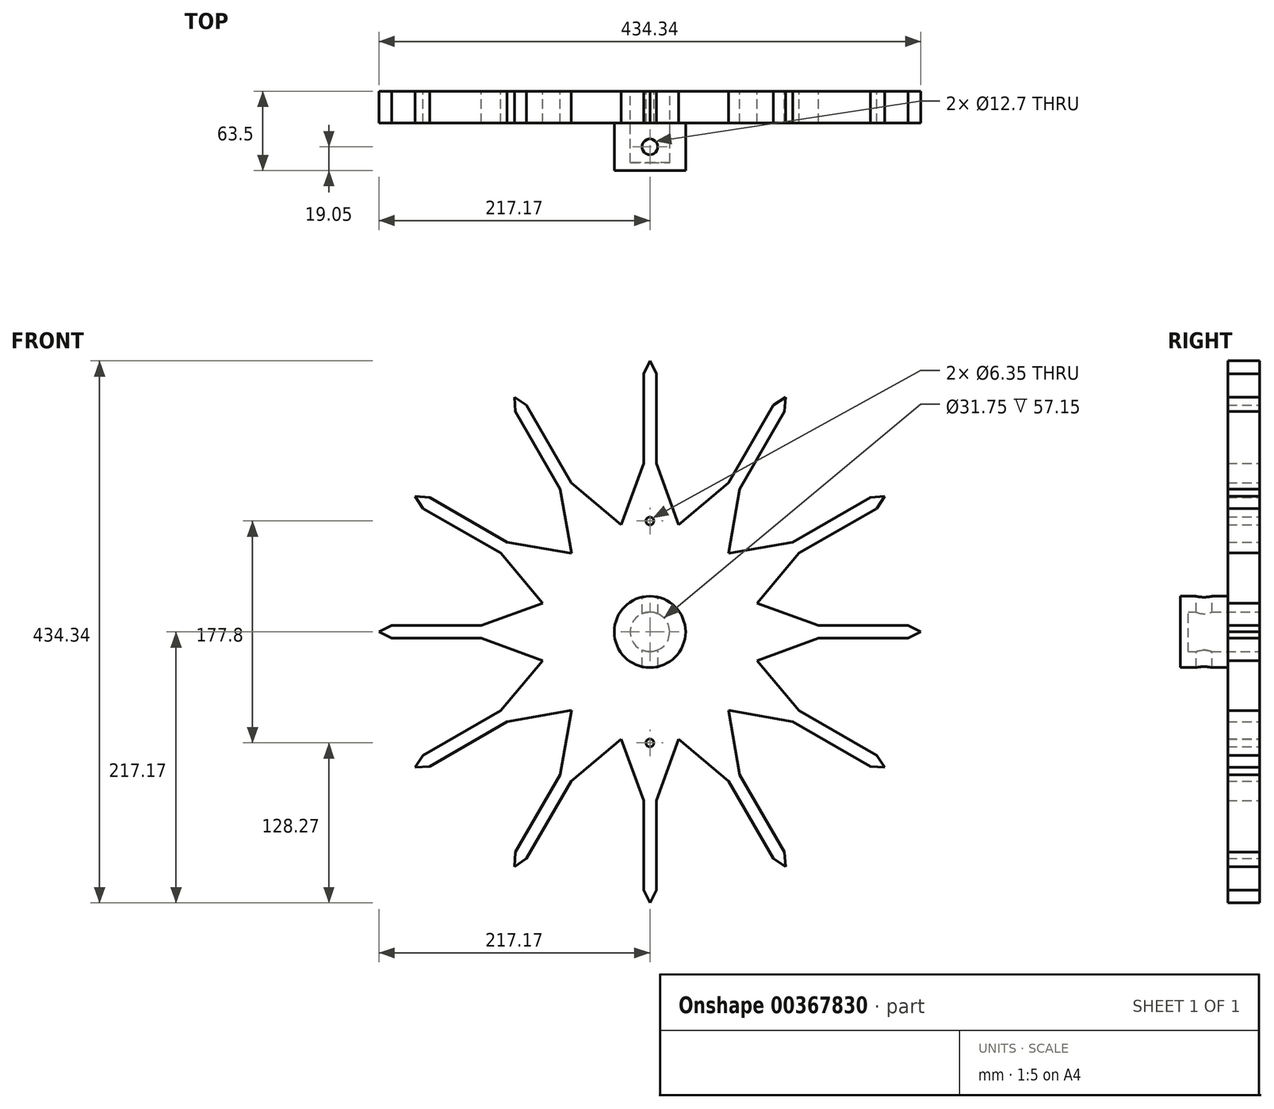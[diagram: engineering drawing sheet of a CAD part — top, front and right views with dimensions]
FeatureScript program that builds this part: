
annotation { "Feature Type Name" : "Feature", "Feature Type Description" : "" }
export const myFeature = defineFeature(function(context is Context, id is Id, definition is map)
    precondition{}
    {
        {
            var Q0;
            Q0=qCreatedBy(makeId("Front.planeOp"),FACE);
            var sketch = newSketch(context, id + "F0", { "sketchPlane" : qUnion([Q0])});
            skCircle(sketch, "E0", {"center": v(0, 0) * mm, "radius": 88.9 * mm});
            skLineSegment(sketch, "E1", {"start": v(0, 88.9) * mm, "end": v(0, 0) * mm, "construction": true});
            skLineSegment(sketch, "E2", {"start": v(44.45, 76.99) * mm, "end": v(0, 0) * mm, "construction": true});
            skLineSegment(sketch, "E3", {"start": v(0, 0) * mm, "end": v(23, 85.87) * mm, "construction": true});
            skCircle(sketch, "E4", {"center": v(0, 0) * mm, "radius": 28.58 * mm});
            skSolve(sketch);
        }
        {
            var Q0;
            Q0=makeQuery(id+"F0.imprint","IMPRINT",FACE,{"disambiguationData":[TD([[makeQuery(id+"F0.imprint","IMPRINT",EDGE,{"derivedFrom":sQuery(id+"F0.wireOp",EDGE,"E0")}),1.0]])]});
            var sketch = newSketch(context, id + "F1", { "sketchPlane" : qUnion([Q0])});
            skLineSegment(sketch, "E5", {"start": v(0, 88.9) * mm, "end": v(0, 217.17) * mm, "construction": true});
            skLineSegment(sketch, "E6.top", {"start": v(5.08, 0) * mm, "end": v(-5.08, 0) * mm});
            skLineSegment(sketch, "E6.left", {"start": v(5.08, 206.78) * mm, "end": v(5.08, 135.13) * mm});
            skLineSegment(sketch, "E6.right", {"start": v(-5.08, 206.78) * mm, "end": v(-5.08, 135.13) * mm});
            skPoint(sketch, "E6.middle", {"position": v(0, 108.59) * mm});
            skLineSegment(sketch, "E7", {"start": v(-5.08, 206.78) * mm, "end": v(0, 217.17) * mm});
            skLineSegment(sketch, "E8", {"start": v(0, 217.17) * mm, "end": v(5.08, 206.78) * mm});
            skPoint(sketch, "E9.orphan", {"position": v(-5.08, 217.17) * mm});
            skPoint(sketch, "E10.orphan", {"position": v(5.08, 217.17) * mm});
            skLineSegment(sketch, "E11", {"start": v(23, 85.87) * mm, "end": v(0, 0) * mm});
            skLineSegment(sketch, "E12", {"start": v(0, 0) * mm, "end": v(0, 108.59) * mm, "construction": true});
            skLineSegment(sketch, "E13", {"start": v(23, 85.87) * mm, "end": v(5.08, 135.13) * mm});
            skLineSegment(sketch, "E14.MirrorCS", {"start": v(-23, 85.87) * mm, "end": v(-5.08, 135.13) * mm});
            skLineSegment(sketch, "E15.MirrorCS", {"start": v(-23, 85.87) * mm, "end": v(0, 0) * mm});
            skLineSegment(sketch, "E16.MirrorCS", {"start": v(-5.08, 0) * mm, "end": v(5.08, 0) * mm});
            skLineSegment(sketch, "E17.MirrorCS", {"start": v(5.08, 206.78) * mm, "end": v(0, 217.17) * mm});
            skLineSegment(sketch, "E18.MirrorCS", {"start": v(0, 217.17) * mm, "end": v(-5.08, 206.78) * mm});
            skPoint(sketch, "E19.orphan", {"position": v(0, 149.09) * mm});
            skLineSegment(sketch, "E20.1.0", {"start": v(-98.99, 181.61) * mm, "end": v(-63.17, 119.57) * mm});
            skLineSegment(sketch, "E20.1.2", {"start": v(-62.86, 62.86) * mm, "end": v(0, 0) * mm});
            skPoint(sketch, "E20.1.3", {"position": v(-112.98, 185.53) * mm});
            skPoint(sketch, "E20.1.4", {"position": v(-104.19, 190.61) * mm});
            skLineSegment(sketch, "E20.1.5", {"start": v(-62.86, 62.86) * mm, "end": v(-71.96, 114.49) * mm});
            skLineSegment(sketch, "E20.1.6", {"start": v(-44.45, 76.99) * mm, "end": v(-108.58, 188.07) * mm, "construction": true});
            skLineSegment(sketch, "E20.1.7", {"start": v(0, 0) * mm, "end": v(-54.3, 94.04) * mm, "construction": true});
            skPoint(sketch, "E20.1.8", {"position": v(-74.54, 129.11) * mm});
            skPoint(sketch, "E20.1.9", {"position": v(-54.3, 94.04) * mm});
            skLineSegment(sketch, "E20.1.10", {"start": v(-107.79, 176.53) * mm, "end": v(-71.96, 114.49) * mm});
            skLineSegment(sketch, "E20.1.11", {"start": v(-98.99, 181.61) * mm, "end": v(-63.17, 119.57) * mm});
            skPoint(sketch, "E20.1.12", {"position": v(-112.98, 185.53) * mm});
            skPoint(sketch, "E20.1.13", {"position": v(-54.3, 94.04) * mm});
            skLineSegment(sketch, "E20.1.15", {"start": v(-62.86, 62.86) * mm, "end": v(0, 0) * mm});
            skLineSegment(sketch, "E20.1.16", {"start": v(-107.79, 176.53) * mm, "end": v(-71.96, 114.49) * mm});
            skPoint(sketch, "E20.1.17", {"position": v(-74.54, 129.11) * mm});
            skLineSegment(sketch, "E20.1.18", {"start": v(0, 0) * mm, "end": v(-54.3, 94.04) * mm, "construction": true});
            skLineSegment(sketch, "E20.1.19", {"start": v(-62.86, 62.86) * mm, "end": v(-71.96, 114.49) * mm});
            skPoint(sketch, "E20.1.20", {"position": v(-104.19, 190.61) * mm});
            skPoint(sketch, "E20.1.21", {"position": v(-74.54, 129.11) * mm});
            skLineSegment(sketch, "E20.1.22", {"start": v(-23, 85.87) * mm, "end": v(-63.17, 119.57) * mm});
            skLineSegment(sketch, "E20.1.23", {"start": v(-23, 85.87) * mm, "end": v(-63.17, 119.57) * mm});
            skPoint(sketch, "E20.1.24", {"position": v(-74.54, 129.11) * mm});
            skLineSegment(sketch, "E20.1.25", {"start": v(-4.4, -2.54) * mm, "end": v(4.4, 2.54) * mm});
            skLineSegment(sketch, "E20.1.26", {"start": v(-98.99, 181.61) * mm, "end": v(-108.59, 188.07) * mm});
            skLineSegment(sketch, "E20.1.27", {"start": v(-107.79, 176.53) * mm, "end": v(-108.58, 188.07) * mm});
            skLineSegment(sketch, "E20.1.28", {"start": v(4.4, 2.54) * mm, "end": v(-4.4, -2.54) * mm});
            skLineSegment(sketch, "E20.1.29", {"start": v(-108.59, 188.07) * mm, "end": v(-107.79, 176.53) * mm});
            skLineSegment(sketch, "E20.1.30", {"start": v(-108.59, 188.07) * mm, "end": v(-98.99, 181.61) * mm});
            skLineSegment(sketch, "E20.2.0", {"start": v(-176.53, 107.79) * mm, "end": v(-114.49, 71.96) * mm});
            skLineSegment(sketch, "E20.2.1", {"start": v(-62.86, 62.86) * mm, "end": v(0, 0) * mm});
            skLineSegment(sketch, "E20.2.2", {"start": v(-85.87, 23) * mm, "end": v(0, 0) * mm});
            skPoint(sketch, "E20.2.3", {"position": v(-190.61, 104.19) * mm});
            skPoint(sketch, "E20.2.4", {"position": v(-185.53, 112.98) * mm});
            skLineSegment(sketch, "E20.2.5", {"start": v(-85.87, 23) * mm, "end": v(-119.57, 63.17) * mm});
            skLineSegment(sketch, "E20.2.6", {"start": v(-76.99, 44.45) * mm, "end": v(-188.07, 108.59) * mm, "construction": true});
            skLineSegment(sketch, "E20.2.7", {"start": v(0, 0) * mm, "end": v(-94.04, 54.3) * mm, "construction": true});
            skPoint(sketch, "E20.2.8", {"position": v(-129.11, 74.54) * mm});
            skPoint(sketch, "E20.2.9", {"position": v(-94.04, 54.3) * mm});
            skLineSegment(sketch, "E20.2.10", {"start": v(-181.61, 98.99) * mm, "end": v(-119.57, 63.17) * mm});
            skLineSegment(sketch, "E20.2.11", {"start": v(-176.53, 107.79) * mm, "end": v(-114.49, 71.96) * mm});
            skPoint(sketch, "E20.2.12", {"position": v(-190.61, 104.19) * mm});
            skPoint(sketch, "E20.2.13", {"position": v(-94.04, 54.3) * mm});
            skLineSegment(sketch, "E20.2.14", {"start": v(-62.86, 62.86) * mm, "end": v(0, 0) * mm});
            skLineSegment(sketch, "E20.2.15", {"start": v(-85.87, 23) * mm, "end": v(0, 0) * mm});
            skLineSegment(sketch, "E20.2.16", {"start": v(-181.61, 98.99) * mm, "end": v(-119.57, 63.17) * mm});
            skPoint(sketch, "E20.2.17", {"position": v(-129.11, 74.54) * mm});
            skLineSegment(sketch, "E20.2.18", {"start": v(0, 0) * mm, "end": v(-94.04, 54.3) * mm, "construction": true});
            skLineSegment(sketch, "E20.2.19", {"start": v(-85.87, 23) * mm, "end": v(-119.57, 63.17) * mm});
            skPoint(sketch, "E20.2.20", {"position": v(-185.53, 112.98) * mm});
            skPoint(sketch, "E20.2.21", {"position": v(-129.11, 74.54) * mm});
            skLineSegment(sketch, "E20.2.22", {"start": v(-62.86, 62.86) * mm, "end": v(-114.49, 71.96) * mm});
            skLineSegment(sketch, "E20.2.23", {"start": v(-62.86, 62.86) * mm, "end": v(-114.49, 71.96) * mm});
            skPoint(sketch, "E20.2.24", {"position": v(-129.11, 74.54) * mm});
            skLineSegment(sketch, "E20.2.25", {"start": v(-2.54, -4.4) * mm, "end": v(2.54, 4.4) * mm});
            skLineSegment(sketch, "E20.2.26", {"start": v(-176.53, 107.79) * mm, "end": v(-188.07, 108.59) * mm});
            skLineSegment(sketch, "E20.2.27", {"start": v(-181.61, 98.99) * mm, "end": v(-188.07, 108.59) * mm});
            skLineSegment(sketch, "E20.2.28", {"start": v(2.54, 4.4) * mm, "end": v(-2.54, -4.4) * mm});
            skLineSegment(sketch, "E20.2.29", {"start": v(-188.07, 108.59) * mm, "end": v(-181.61, 98.99) * mm});
            skLineSegment(sketch, "E20.2.30", {"start": v(-188.07, 108.59) * mm, "end": v(-176.53, 107.79) * mm});
            skLineSegment(sketch, "E20.3.0", {"start": v(-206.78, 5.08) * mm, "end": v(-135.13, 5.08) * mm});
            skLineSegment(sketch, "E20.3.1", {"start": v(-85.87, 23) * mm, "end": v(0, 0) * mm});
            skLineSegment(sketch, "E20.3.2", {"start": v(-85.87, -23) * mm, "end": v(0, 0) * mm});
            skPoint(sketch, "E20.3.3", {"position": v(-217.17, -5.08) * mm});
            skPoint(sketch, "E20.3.4", {"position": v(-217.17, 5.08) * mm});
            skLineSegment(sketch, "E20.3.5", {"start": v(-85.87, -23) * mm, "end": v(-135.13, -5.08) * mm});
            skLineSegment(sketch, "E20.3.6", {"start": v(-88.9, 0) * mm, "end": v(-217.17, 0) * mm, "construction": true});
            skLineSegment(sketch, "E20.3.7", {"start": v(0, 0) * mm, "end": v(-108.59, 0) * mm, "construction": true});
            skPoint(sketch, "E20.3.8", {"position": v(-149.09, 0) * mm});
            skPoint(sketch, "E20.3.9", {"position": v(-108.59, 0) * mm});
            skLineSegment(sketch, "E20.3.10", {"start": v(-206.78, -5.08) * mm, "end": v(-135.13, -5.08) * mm});
            skLineSegment(sketch, "E20.3.11", {"start": v(-206.78, 5.08) * mm, "end": v(-135.13, 5.08) * mm});
            skPoint(sketch, "E20.3.12", {"position": v(-217.17, -5.08) * mm});
            skPoint(sketch, "E20.3.13", {"position": v(-108.59, 0) * mm});
            skLineSegment(sketch, "E20.3.14", {"start": v(-85.87, 23) * mm, "end": v(0, 0) * mm});
            skLineSegment(sketch, "E20.3.15", {"start": v(-85.87, -23) * mm, "end": v(0, 0) * mm});
            skLineSegment(sketch, "E20.3.16", {"start": v(-206.78, -5.08) * mm, "end": v(-135.13, -5.08) * mm});
            skPoint(sketch, "E20.3.17", {"position": v(-149.09, 0) * mm});
            skLineSegment(sketch, "E20.3.18", {"start": v(0, 0) * mm, "end": v(-108.59, 0) * mm, "construction": true});
            skLineSegment(sketch, "E20.3.19", {"start": v(-85.87, -23) * mm, "end": v(-135.13, -5.08) * mm});
            skPoint(sketch, "E20.3.20", {"position": v(-217.17, 5.08) * mm});
            skPoint(sketch, "E20.3.21", {"position": v(-149.09, 0) * mm});
            skLineSegment(sketch, "E20.3.22", {"start": v(-85.87, 23) * mm, "end": v(-135.13, 5.08) * mm});
            skLineSegment(sketch, "E20.3.23", {"start": v(-85.87, 23) * mm, "end": v(-135.13, 5.08) * mm});
            skPoint(sketch, "E20.3.24", {"position": v(-149.09, 0) * mm});
            skLineSegment(sketch, "E20.3.25", {"start": v(0, -5.08) * mm, "end": v(0, 5.08) * mm});
            skLineSegment(sketch, "E20.3.26", {"start": v(-206.78, 5.08) * mm, "end": v(-217.17, 0) * mm});
            skLineSegment(sketch, "E20.3.27", {"start": v(-206.78, -5.08) * mm, "end": v(-217.17, 0) * mm});
            skLineSegment(sketch, "E20.3.28", {"start": v(0, 5.08) * mm, "end": v(0, -5.08) * mm});
            skLineSegment(sketch, "E20.3.29", {"start": v(-217.17, 0) * mm, "end": v(-206.78, -5.08) * mm});
            skLineSegment(sketch, "E20.3.30", {"start": v(-217.17, 0) * mm, "end": v(-206.78, 5.08) * mm});
            skLineSegment(sketch, "E20.4.0", {"start": v(-181.61, -98.99) * mm, "end": v(-119.57, -63.17) * mm});
            skLineSegment(sketch, "E20.4.1", {"start": v(-85.87, -23) * mm, "end": v(0, 0) * mm});
            skLineSegment(sketch, "E20.4.2", {"start": v(-62.86, -62.86) * mm, "end": v(0, 0) * mm});
            skPoint(sketch, "E20.4.3", {"position": v(-185.53, -112.98) * mm});
            skPoint(sketch, "E20.4.4", {"position": v(-190.61, -104.19) * mm});
            skLineSegment(sketch, "E20.4.5", {"start": v(-62.86, -62.86) * mm, "end": v(-114.49, -71.96) * mm});
            skLineSegment(sketch, "E20.4.6", {"start": v(-76.99, -44.45) * mm, "end": v(-188.07, -108.59) * mm, "construction": true});
            skLineSegment(sketch, "E20.4.7", {"start": v(0, 0) * mm, "end": v(-94.04, -54.3) * mm, "construction": true});
            skPoint(sketch, "E20.4.8", {"position": v(-129.11, -74.54) * mm});
            skPoint(sketch, "E20.4.9", {"position": v(-94.04, -54.3) * mm});
            skLineSegment(sketch, "E20.4.10", {"start": v(-176.53, -107.79) * mm, "end": v(-114.49, -71.96) * mm});
            skLineSegment(sketch, "E20.4.11", {"start": v(-181.61, -98.99) * mm, "end": v(-119.57, -63.17) * mm});
            skPoint(sketch, "E20.4.12", {"position": v(-185.53, -112.98) * mm});
            skPoint(sketch, "E20.4.13", {"position": v(-94.04, -54.3) * mm});
            skLineSegment(sketch, "E20.4.14", {"start": v(-85.87, -23) * mm, "end": v(0, 0) * mm});
            skLineSegment(sketch, "E20.4.15", {"start": v(-62.86, -62.86) * mm, "end": v(0, 0) * mm});
            skLineSegment(sketch, "E20.4.16", {"start": v(-176.53, -107.79) * mm, "end": v(-114.49, -71.96) * mm});
            skPoint(sketch, "E20.4.17", {"position": v(-129.11, -74.54) * mm});
            skLineSegment(sketch, "E20.4.18", {"start": v(0, 0) * mm, "end": v(-94.04, -54.3) * mm, "construction": true});
            skLineSegment(sketch, "E20.4.19", {"start": v(-62.86, -62.86) * mm, "end": v(-114.49, -71.96) * mm});
            skPoint(sketch, "E20.4.20", {"position": v(-190.61, -104.19) * mm});
            skPoint(sketch, "E20.4.21", {"position": v(-129.11, -74.54) * mm});
            skLineSegment(sketch, "E20.4.22", {"start": v(-85.87, -23) * mm, "end": v(-119.57, -63.17) * mm});
            skLineSegment(sketch, "E20.4.23", {"start": v(-85.87, -23) * mm, "end": v(-119.57, -63.17) * mm});
            skPoint(sketch, "E20.4.24", {"position": v(-129.11, -74.54) * mm});
            skLineSegment(sketch, "E20.4.25", {"start": v(2.54, -4.4) * mm, "end": v(-2.54, 4.4) * mm});
            skLineSegment(sketch, "E20.4.26", {"start": v(-181.61, -98.99) * mm, "end": v(-188.07, -108.58) * mm});
            skLineSegment(sketch, "E20.4.27", {"start": v(-176.53, -107.79) * mm, "end": v(-188.07, -108.58) * mm});
            skLineSegment(sketch, "E20.4.28", {"start": v(-2.54, 4.4) * mm, "end": v(2.54, -4.4) * mm});
            skLineSegment(sketch, "E20.4.29", {"start": v(-188.07, -108.58) * mm, "end": v(-176.53, -107.79) * mm});
            skLineSegment(sketch, "E20.4.30", {"start": v(-188.07, -108.58) * mm, "end": v(-181.61, -98.99) * mm});
            skLineSegment(sketch, "E20.5.0", {"start": v(-107.79, -176.53) * mm, "end": v(-71.96, -114.49) * mm});
            skLineSegment(sketch, "E20.5.1", {"start": v(-62.86, -62.86) * mm, "end": v(0, 0) * mm});
            skLineSegment(sketch, "E20.5.2", {"start": v(-23, -85.87) * mm, "end": v(0, 0) * mm});
            skPoint(sketch, "E20.5.3", {"position": v(-104.19, -190.61) * mm});
            skPoint(sketch, "E20.5.4", {"position": v(-112.98, -185.53) * mm});
            skLineSegment(sketch, "E20.5.5", {"start": v(-23, -85.87) * mm, "end": v(-63.17, -119.57) * mm});
            skLineSegment(sketch, "E20.5.6", {"start": v(-44.45, -76.99) * mm, "end": v(-108.58, -188.07) * mm, "construction": true});
            skLineSegment(sketch, "E20.5.7", {"start": v(0, 0) * mm, "end": v(-54.3, -94.04) * mm, "construction": true});
            skPoint(sketch, "E20.5.8", {"position": v(-74.54, -129.11) * mm});
            skPoint(sketch, "E20.5.9", {"position": v(-54.3, -94.04) * mm});
            skLineSegment(sketch, "E20.5.10", {"start": v(-98.99, -181.61) * mm, "end": v(-63.17, -119.57) * mm});
            skLineSegment(sketch, "E20.5.11", {"start": v(-107.79, -176.53) * mm, "end": v(-71.96, -114.49) * mm});
            skPoint(sketch, "E20.5.12", {"position": v(-104.19, -190.61) * mm});
            skPoint(sketch, "E20.5.13", {"position": v(-54.3, -94.04) * mm});
            skLineSegment(sketch, "E20.5.14", {"start": v(-62.86, -62.86) * mm, "end": v(0, 0) * mm});
            skLineSegment(sketch, "E20.5.15", {"start": v(-23, -85.87) * mm, "end": v(0, 0) * mm});
            skLineSegment(sketch, "E20.5.16", {"start": v(-98.99, -181.61) * mm, "end": v(-63.17, -119.57) * mm});
            skPoint(sketch, "E20.5.17", {"position": v(-74.54, -129.11) * mm});
            skLineSegment(sketch, "E20.5.18", {"start": v(0, 0) * mm, "end": v(-54.3, -94.04) * mm, "construction": true});
            skLineSegment(sketch, "E20.5.19", {"start": v(-23, -85.87) * mm, "end": v(-63.17, -119.57) * mm});
            skPoint(sketch, "E20.5.20", {"position": v(-112.98, -185.53) * mm});
            skPoint(sketch, "E20.5.21", {"position": v(-74.54, -129.11) * mm});
            skLineSegment(sketch, "E20.5.22", {"start": v(-62.86, -62.86) * mm, "end": v(-71.96, -114.49) * mm});
            skLineSegment(sketch, "E20.5.23", {"start": v(-62.86, -62.86) * mm, "end": v(-71.96, -114.49) * mm});
            skPoint(sketch, "E20.5.24", {"position": v(-74.54, -129.11) * mm});
            skLineSegment(sketch, "E20.5.25", {"start": v(4.4, -2.54) * mm, "end": v(-4.4, 2.54) * mm});
            skLineSegment(sketch, "E20.5.26", {"start": v(-107.79, -176.53) * mm, "end": v(-108.58, -188.07) * mm});
            skLineSegment(sketch, "E20.5.27", {"start": v(-98.99, -181.61) * mm, "end": v(-108.59, -188.07) * mm});
            skLineSegment(sketch, "E20.5.28", {"start": v(-4.4, 2.54) * mm, "end": v(4.4, -2.54) * mm});
            skLineSegment(sketch, "E20.5.29", {"start": v(-108.59, -188.07) * mm, "end": v(-98.99, -181.61) * mm});
            skLineSegment(sketch, "E20.5.30", {"start": v(-108.59, -188.07) * mm, "end": v(-107.79, -176.53) * mm});
            skLineSegment(sketch, "E20.6.0", {"start": v(-5.08, -206.78) * mm, "end": v(-5.08, -135.13) * mm});
            skLineSegment(sketch, "E20.6.1", {"start": v(-23, -85.87) * mm, "end": v(0, 0) * mm});
            skLineSegment(sketch, "E20.6.2", {"start": v(23, -85.87) * mm, "end": v(0, 0) * mm});
            skPoint(sketch, "E20.6.3", {"position": v(5.08, -217.17) * mm});
            skPoint(sketch, "E20.6.4", {"position": v(-5.08, -217.17) * mm});
            skLineSegment(sketch, "E20.6.5", {"start": v(23, -85.87) * mm, "end": v(5.08, -135.13) * mm});
            skLineSegment(sketch, "E20.6.6", {"start": v(0, -88.9) * mm, "end": v(0, -217.17) * mm, "construction": true});
            skLineSegment(sketch, "E20.6.7", {"start": v(0, 0) * mm, "end": v(0, -108.59) * mm, "construction": true});
            skPoint(sketch, "E20.6.8", {"position": v(0, -149.09) * mm});
            skPoint(sketch, "E20.6.9", {"position": v(0, -108.59) * mm});
            skLineSegment(sketch, "E20.6.10", {"start": v(5.08, -206.78) * mm, "end": v(5.08, -135.13) * mm});
            skLineSegment(sketch, "E20.6.11", {"start": v(-5.08, -206.78) * mm, "end": v(-5.08, -135.13) * mm});
            skPoint(sketch, "E20.6.12", {"position": v(5.08, -217.17) * mm});
            skPoint(sketch, "E20.6.13", {"position": v(0, -108.59) * mm});
            skLineSegment(sketch, "E20.6.14", {"start": v(-23, -85.87) * mm, "end": v(0, 0) * mm});
            skLineSegment(sketch, "E20.6.15", {"start": v(23, -85.87) * mm, "end": v(0, 0) * mm});
            skLineSegment(sketch, "E20.6.16", {"start": v(5.08, -206.78) * mm, "end": v(5.08, -135.13) * mm});
            skPoint(sketch, "E20.6.17", {"position": v(0, -149.09) * mm});
            skLineSegment(sketch, "E20.6.18", {"start": v(0, 0) * mm, "end": v(0, -108.59) * mm, "construction": true});
            skLineSegment(sketch, "E20.6.19", {"start": v(23, -85.87) * mm, "end": v(5.08, -135.13) * mm});
            skPoint(sketch, "E20.6.20", {"position": v(-5.08, -217.17) * mm});
            skPoint(sketch, "E20.6.21", {"position": v(0, -149.09) * mm});
            skLineSegment(sketch, "E20.6.22", {"start": v(-23, -85.87) * mm, "end": v(-5.08, -135.13) * mm});
            skLineSegment(sketch, "E20.6.23", {"start": v(-23, -85.87) * mm, "end": v(-5.08, -135.13) * mm});
            skPoint(sketch, "E20.6.24", {"position": v(0, -149.09) * mm});
            skLineSegment(sketch, "E20.6.26", {"start": v(-5.08, -206.78) * mm, "end": v(0, -217.17) * mm});
            skLineSegment(sketch, "E20.6.27", {"start": v(5.08, -206.78) * mm, "end": v(0, -217.17) * mm});
            skLineSegment(sketch, "E20.6.29", {"start": v(0, -217.17) * mm, "end": v(5.08, -206.78) * mm});
            skLineSegment(sketch, "E20.6.30", {"start": v(0, -217.17) * mm, "end": v(-5.08, -206.78) * mm});
            skLineSegment(sketch, "E20.7.0", {"start": v(98.99, -181.61) * mm, "end": v(63.17, -119.57) * mm});
            skLineSegment(sketch, "E20.7.1", {"start": v(23, -85.87) * mm, "end": v(0, 0) * mm});
            skLineSegment(sketch, "E20.7.2", {"start": v(62.86, -62.86) * mm, "end": v(0, 0) * mm});
            skPoint(sketch, "E20.7.3", {"position": v(112.98, -185.53) * mm});
            skPoint(sketch, "E20.7.4", {"position": v(104.19, -190.61) * mm});
            skLineSegment(sketch, "E20.7.5", {"start": v(62.86, -62.86) * mm, "end": v(71.96, -114.49) * mm});
            skLineSegment(sketch, "E20.7.6", {"start": v(44.45, -76.99) * mm, "end": v(108.58, -188.07) * mm, "construction": true});
            skLineSegment(sketch, "E20.7.7", {"start": v(0, 0) * mm, "end": v(54.3, -94.04) * mm, "construction": true});
            skPoint(sketch, "E20.7.8", {"position": v(74.54, -129.11) * mm});
            skPoint(sketch, "E20.7.9", {"position": v(54.3, -94.04) * mm});
            skLineSegment(sketch, "E20.7.10", {"start": v(107.79, -176.53) * mm, "end": v(71.96, -114.49) * mm});
            skLineSegment(sketch, "E20.7.11", {"start": v(98.99, -181.61) * mm, "end": v(63.17, -119.57) * mm});
            skPoint(sketch, "E20.7.12", {"position": v(112.98, -185.53) * mm});
            skPoint(sketch, "E20.7.13", {"position": v(54.3, -94.04) * mm});
            skLineSegment(sketch, "E20.7.14", {"start": v(23, -85.87) * mm, "end": v(0, 0) * mm});
            skLineSegment(sketch, "E20.7.15", {"start": v(62.86, -62.86) * mm, "end": v(0, 0) * mm});
            skLineSegment(sketch, "E20.7.16", {"start": v(107.79, -176.53) * mm, "end": v(71.96, -114.49) * mm});
            skPoint(sketch, "E20.7.17", {"position": v(74.54, -129.11) * mm});
            skLineSegment(sketch, "E20.7.18", {"start": v(0, 0) * mm, "end": v(54.3, -94.04) * mm, "construction": true});
            skLineSegment(sketch, "E20.7.19", {"start": v(62.86, -62.86) * mm, "end": v(71.96, -114.49) * mm});
            skPoint(sketch, "E20.7.20", {"position": v(104.19, -190.61) * mm});
            skPoint(sketch, "E20.7.21", {"position": v(74.54, -129.11) * mm});
            skLineSegment(sketch, "E20.7.22", {"start": v(23, -85.87) * mm, "end": v(63.17, -119.57) * mm});
            skLineSegment(sketch, "E20.7.23", {"start": v(23, -85.87) * mm, "end": v(63.17, -119.57) * mm});
            skPoint(sketch, "E20.7.24", {"position": v(74.54, -129.11) * mm});
            skLineSegment(sketch, "E20.7.25", {"start": v(4.4, 2.54) * mm, "end": v(-4.4, -2.54) * mm});
            skLineSegment(sketch, "E20.7.26", {"start": v(98.99, -181.61) * mm, "end": v(108.58, -188.07) * mm});
            skLineSegment(sketch, "E20.7.27", {"start": v(107.79, -176.53) * mm, "end": v(108.58, -188.07) * mm});
            skLineSegment(sketch, "E20.7.28", {"start": v(-4.4, -2.54) * mm, "end": v(4.4, 2.54) * mm});
            skLineSegment(sketch, "E20.7.29", {"start": v(108.58, -188.07) * mm, "end": v(107.79, -176.53) * mm});
            skLineSegment(sketch, "E20.7.30", {"start": v(108.58, -188.07) * mm, "end": v(98.99, -181.61) * mm});
            skLineSegment(sketch, "E20.8.0", {"start": v(176.53, -107.79) * mm, "end": v(114.49, -71.96) * mm});
            skLineSegment(sketch, "E20.8.1", {"start": v(62.86, -62.86) * mm, "end": v(0, 0) * mm});
            skLineSegment(sketch, "E20.8.2", {"start": v(85.87, -23) * mm, "end": v(0, 0) * mm});
            skPoint(sketch, "E20.8.3", {"position": v(190.61, -104.19) * mm});
            skPoint(sketch, "E20.8.4", {"position": v(185.53, -112.98) * mm});
            skLineSegment(sketch, "E20.8.5", {"start": v(85.87, -23) * mm, "end": v(119.57, -63.17) * mm});
            skLineSegment(sketch, "E20.8.6", {"start": v(76.99, -44.45) * mm, "end": v(188.07, -108.59) * mm, "construction": true});
            skLineSegment(sketch, "E20.8.7", {"start": v(0, 0) * mm, "end": v(94.04, -54.3) * mm, "construction": true});
            skPoint(sketch, "E20.8.8", {"position": v(129.11, -74.54) * mm});
            skPoint(sketch, "E20.8.9", {"position": v(94.04, -54.3) * mm});
            skLineSegment(sketch, "E20.8.10", {"start": v(181.61, -98.99) * mm, "end": v(119.57, -63.17) * mm});
            skLineSegment(sketch, "E20.8.11", {"start": v(176.53, -107.79) * mm, "end": v(114.49, -71.96) * mm});
            skPoint(sketch, "E20.8.12", {"position": v(190.61, -104.19) * mm});
            skPoint(sketch, "E20.8.13", {"position": v(94.04, -54.3) * mm});
            skLineSegment(sketch, "E20.8.14", {"start": v(62.86, -62.86) * mm, "end": v(0, 0) * mm});
            skLineSegment(sketch, "E20.8.15", {"start": v(85.87, -23) * mm, "end": v(0, 0) * mm});
            skLineSegment(sketch, "E20.8.16", {"start": v(181.61, -98.99) * mm, "end": v(119.57, -63.17) * mm});
            skPoint(sketch, "E20.8.17", {"position": v(129.11, -74.54) * mm});
            skLineSegment(sketch, "E20.8.18", {"start": v(0, 0) * mm, "end": v(94.04, -54.3) * mm, "construction": true});
            skLineSegment(sketch, "E20.8.19", {"start": v(85.87, -23) * mm, "end": v(119.57, -63.17) * mm});
            skPoint(sketch, "E20.8.20", {"position": v(185.53, -112.98) * mm});
            skPoint(sketch, "E20.8.21", {"position": v(129.11, -74.54) * mm});
            skLineSegment(sketch, "E20.8.22", {"start": v(62.86, -62.86) * mm, "end": v(114.49, -71.96) * mm});
            skLineSegment(sketch, "E20.8.23", {"start": v(62.86, -62.86) * mm, "end": v(114.49, -71.96) * mm});
            skPoint(sketch, "E20.8.24", {"position": v(129.11, -74.54) * mm});
            skLineSegment(sketch, "E20.8.25", {"start": v(2.54, 4.4) * mm, "end": v(-2.54, -4.4) * mm});
            skLineSegment(sketch, "E20.8.26", {"start": v(176.53, -107.79) * mm, "end": v(188.07, -108.59) * mm});
            skLineSegment(sketch, "E20.8.27", {"start": v(181.61, -98.99) * mm, "end": v(188.07, -108.59) * mm});
            skLineSegment(sketch, "E20.8.28", {"start": v(-2.54, -4.4) * mm, "end": v(2.54, 4.4) * mm});
            skLineSegment(sketch, "E20.8.29", {"start": v(188.07, -108.59) * mm, "end": v(181.61, -98.99) * mm});
            skLineSegment(sketch, "E20.8.30", {"start": v(188.07, -108.59) * mm, "end": v(176.53, -107.79) * mm});
            skLineSegment(sketch, "E20.9.0", {"start": v(206.78, -5.08) * mm, "end": v(135.13, -5.08) * mm});
            skLineSegment(sketch, "E20.9.1", {"start": v(85.87, -23) * mm, "end": v(0, 0) * mm});
            skLineSegment(sketch, "E20.9.2", {"start": v(85.87, 23) * mm, "end": v(0, 0) * mm});
            skPoint(sketch, "E20.9.3", {"position": v(217.17, 5.08) * mm});
            skPoint(sketch, "E20.9.4", {"position": v(217.17, -5.08) * mm});
            skLineSegment(sketch, "E20.9.5", {"start": v(85.87, 23) * mm, "end": v(135.13, 5.08) * mm});
            skLineSegment(sketch, "E20.9.6", {"start": v(88.9, 0) * mm, "end": v(217.17, 0) * mm, "construction": true});
            skLineSegment(sketch, "E20.9.7", {"start": v(0, 0) * mm, "end": v(108.59, 0) * mm, "construction": true});
            skPoint(sketch, "E20.9.8", {"position": v(149.09, 0) * mm});
            skPoint(sketch, "E20.9.9", {"position": v(108.59, 0) * mm});
            skLineSegment(sketch, "E20.9.10", {"start": v(206.78, 5.08) * mm, "end": v(135.13, 5.08) * mm});
            skLineSegment(sketch, "E20.9.11", {"start": v(206.78, -5.08) * mm, "end": v(135.13, -5.08) * mm});
            skPoint(sketch, "E20.9.12", {"position": v(217.17, 5.08) * mm});
            skPoint(sketch, "E20.9.13", {"position": v(108.59, 0) * mm});
            skLineSegment(sketch, "E20.9.14", {"start": v(85.87, -23) * mm, "end": v(0, 0) * mm});
            skLineSegment(sketch, "E20.9.15", {"start": v(85.87, 23) * mm, "end": v(0, 0) * mm});
            skLineSegment(sketch, "E20.9.16", {"start": v(206.78, 5.08) * mm, "end": v(135.13, 5.08) * mm});
            skPoint(sketch, "E20.9.17", {"position": v(149.09, 0) * mm});
            skLineSegment(sketch, "E20.9.18", {"start": v(0, 0) * mm, "end": v(108.59, 0) * mm, "construction": true});
            skLineSegment(sketch, "E20.9.19", {"start": v(85.87, 23) * mm, "end": v(135.13, 5.08) * mm});
            skPoint(sketch, "E20.9.20", {"position": v(217.17, -5.08) * mm});
            skPoint(sketch, "E20.9.21", {"position": v(149.09, 0) * mm});
            skLineSegment(sketch, "E20.9.22", {"start": v(85.87, -23) * mm, "end": v(135.13, -5.08) * mm});
            skLineSegment(sketch, "E20.9.23", {"start": v(85.87, -23) * mm, "end": v(135.13, -5.08) * mm});
            skPoint(sketch, "E20.9.24", {"position": v(149.09, 0) * mm});
            skLineSegment(sketch, "E20.9.25", {"start": v(0, 5.08) * mm, "end": v(0, -5.08) * mm});
            skLineSegment(sketch, "E20.9.26", {"start": v(206.78, -5.08) * mm, "end": v(217.17, 0) * mm});
            skLineSegment(sketch, "E20.9.27", {"start": v(206.78, 5.08) * mm, "end": v(217.17, 0) * mm});
            skLineSegment(sketch, "E20.9.28", {"start": v(0, -5.08) * mm, "end": v(0, 5.08) * mm});
            skLineSegment(sketch, "E20.9.29", {"start": v(217.17, 0) * mm, "end": v(206.78, 5.08) * mm});
            skLineSegment(sketch, "E20.9.30", {"start": v(217.17, 0) * mm, "end": v(206.78, -5.08) * mm});
            skLineSegment(sketch, "E20.10.0", {"start": v(181.61, 98.99) * mm, "end": v(119.57, 63.17) * mm});
            skLineSegment(sketch, "E20.10.1", {"start": v(85.87, 23) * mm, "end": v(0, 0) * mm});
            skLineSegment(sketch, "E20.10.2", {"start": v(62.86, 62.86) * mm, "end": v(0, 0) * mm});
            skPoint(sketch, "E20.10.3", {"position": v(185.53, 112.98) * mm});
            skPoint(sketch, "E20.10.4", {"position": v(190.61, 104.19) * mm});
            skLineSegment(sketch, "E20.10.5", {"start": v(62.86, 62.86) * mm, "end": v(114.49, 71.96) * mm});
            skLineSegment(sketch, "E20.10.6", {"start": v(76.99, 44.45) * mm, "end": v(188.07, 108.59) * mm, "construction": true});
            skLineSegment(sketch, "E20.10.7", {"start": v(0, 0) * mm, "end": v(94.04, 54.3) * mm, "construction": true});
            skPoint(sketch, "E20.10.8", {"position": v(129.11, 74.54) * mm});
            skPoint(sketch, "E20.10.9", {"position": v(94.04, 54.3) * mm});
            skLineSegment(sketch, "E20.10.10", {"start": v(176.53, 107.79) * mm, "end": v(114.49, 71.96) * mm});
            skLineSegment(sketch, "E20.10.11", {"start": v(181.61, 98.99) * mm, "end": v(119.57, 63.17) * mm});
            skPoint(sketch, "E20.10.12", {"position": v(185.53, 112.98) * mm});
            skPoint(sketch, "E20.10.13", {"position": v(94.04, 54.3) * mm});
            skLineSegment(sketch, "E20.10.14", {"start": v(85.87, 23) * mm, "end": v(0, 0) * mm});
            skLineSegment(sketch, "E20.10.15", {"start": v(62.86, 62.86) * mm, "end": v(0, 0) * mm});
            skLineSegment(sketch, "E20.10.16", {"start": v(176.53, 107.79) * mm, "end": v(114.49, 71.96) * mm});
            skPoint(sketch, "E20.10.17", {"position": v(129.11, 74.54) * mm});
            skLineSegment(sketch, "E20.10.18", {"start": v(0, 0) * mm, "end": v(94.04, 54.3) * mm, "construction": true});
            skLineSegment(sketch, "E20.10.19", {"start": v(62.86, 62.86) * mm, "end": v(114.49, 71.96) * mm});
            skPoint(sketch, "E20.10.20", {"position": v(190.61, 104.19) * mm});
            skPoint(sketch, "E20.10.21", {"position": v(129.11, 74.54) * mm});
            skLineSegment(sketch, "E20.10.22", {"start": v(85.87, 23) * mm, "end": v(119.57, 63.17) * mm});
            skLineSegment(sketch, "E20.10.23", {"start": v(85.87, 23) * mm, "end": v(119.57, 63.17) * mm});
            skPoint(sketch, "E20.10.24", {"position": v(129.11, 74.54) * mm});
            skLineSegment(sketch, "E20.10.25", {"start": v(-2.54, 4.4) * mm, "end": v(2.54, -4.4) * mm});
            skLineSegment(sketch, "E20.10.26", {"start": v(181.61, 98.99) * mm, "end": v(188.07, 108.59) * mm});
            skLineSegment(sketch, "E20.10.27", {"start": v(176.53, 107.79) * mm, "end": v(188.07, 108.59) * mm});
            skLineSegment(sketch, "E20.10.28", {"start": v(2.54, -4.4) * mm, "end": v(-2.54, 4.4) * mm});
            skLineSegment(sketch, "E20.10.29", {"start": v(188.07, 108.59) * mm, "end": v(176.53, 107.79) * mm});
            skLineSegment(sketch, "E20.10.30", {"start": v(188.07, 108.59) * mm, "end": v(181.61, 98.99) * mm});
            skLineSegment(sketch, "E20.11.0", {"start": v(107.79, 176.53) * mm, "end": v(71.96, 114.49) * mm});
            skLineSegment(sketch, "E20.11.1", {"start": v(62.86, 62.86) * mm, "end": v(0, 0) * mm});
            skPoint(sketch, "E20.11.3", {"position": v(104.19, 190.61) * mm});
            skPoint(sketch, "E20.11.4", {"position": v(112.98, 185.53) * mm});
            skLineSegment(sketch, "E20.11.5", {"start": v(23, 85.87) * mm, "end": v(63.17, 119.57) * mm});
            skLineSegment(sketch, "E20.11.6", {"start": v(44.45, 76.99) * mm, "end": v(108.59, 188.07) * mm, "construction": true});
            skLineSegment(sketch, "E20.11.7", {"start": v(0, 0) * mm, "end": v(54.3, 94.04) * mm, "construction": true});
            skPoint(sketch, "E20.11.8", {"position": v(74.54, 129.11) * mm});
            skPoint(sketch, "E20.11.9", {"position": v(54.3, 94.04) * mm});
            skLineSegment(sketch, "E20.11.10", {"start": v(98.99, 181.61) * mm, "end": v(63.17, 119.57) * mm});
            skLineSegment(sketch, "E20.11.11", {"start": v(107.79, 176.53) * mm, "end": v(71.96, 114.49) * mm});
            skPoint(sketch, "E20.11.12", {"position": v(104.19, 190.61) * mm});
            skPoint(sketch, "E20.11.13", {"position": v(54.3, 94.04) * mm});
            skLineSegment(sketch, "E20.11.14", {"start": v(62.86, 62.86) * mm, "end": v(0, 0) * mm});
            skLineSegment(sketch, "E20.11.16", {"start": v(98.99, 181.61) * mm, "end": v(63.17, 119.57) * mm});
            skPoint(sketch, "E20.11.17", {"position": v(74.54, 129.11) * mm});
            skLineSegment(sketch, "E20.11.18", {"start": v(0, 0) * mm, "end": v(54.3, 94.04) * mm, "construction": true});
            skLineSegment(sketch, "E20.11.19", {"start": v(23, 85.87) * mm, "end": v(63.17, 119.57) * mm});
            skPoint(sketch, "E20.11.20", {"position": v(112.98, 185.53) * mm});
            skPoint(sketch, "E20.11.21", {"position": v(74.54, 129.11) * mm});
            skLineSegment(sketch, "E20.11.22", {"start": v(62.86, 62.86) * mm, "end": v(71.96, 114.49) * mm});
            skLineSegment(sketch, "E20.11.23", {"start": v(62.86, 62.86) * mm, "end": v(71.96, 114.49) * mm});
            skPoint(sketch, "E20.11.24", {"position": v(74.54, 129.11) * mm});
            skLineSegment(sketch, "E20.11.25", {"start": v(-4.4, 2.54) * mm, "end": v(4.4, -2.54) * mm});
            skLineSegment(sketch, "E20.11.26", {"start": v(107.79, 176.53) * mm, "end": v(108.59, 188.07) * mm});
            skLineSegment(sketch, "E20.11.27", {"start": v(98.99, 181.61) * mm, "end": v(108.59, 188.07) * mm});
            skLineSegment(sketch, "E20.11.28", {"start": v(4.4, -2.54) * mm, "end": v(-4.4, 2.54) * mm});
            skLineSegment(sketch, "E20.11.29", {"start": v(108.59, 188.07) * mm, "end": v(98.99, 181.61) * mm});
            skLineSegment(sketch, "E20.11.30", {"start": v(108.59, 188.07) * mm, "end": v(107.79, 176.53) * mm});
            skPoint(sketch, "E20.center", {"position": v(0, 0) * mm});
            skSolve(sketch);
        }
        {
            var Q0;
            Q0=qSketchRegion(id+"F1",true);
            extrude(context, id + "F2", {"entities" : qUnion([Q0]), "depth" : 25.4 * mm});
        }
        {
            var Q0;
            Q0=makeQuery(id+"F0.imprint","IMPRINT",FACE,{"disambiguationData":[TD([[makeQuery(id+"F0.imprint","IMPRINT",EDGE,{"derivedFrom":sQuery(id+"F0.wireOp",EDGE,"E0")}),1.0]])]});
            var sketch = newSketch(context, id + "F3", { "sketchPlane" : qUnion([Q0])});
            skCircle(sketch, "E21", {"center": v(0, 0) * mm, "radius": 28.57 * mm});
            skSolve(sketch);
        }
        {
            var Q0;
            Q0=qSketchRegion(id+"F3",true);
            extrude(context, id + "F4", {"entities" : qUnion([Q0]), "operationType" : NewBodyOperationType.ADD, "depth" : 63.5 * mm});
        }
        {
            var Q0;
            Q0=makeQuery(id+"F0.imprint","IMPRINT",FACE,{"disambiguationData":[TD([[makeQuery(id+"F0.imprint","IMPRINT",EDGE,{"derivedFrom":sQuery(id+"F0.wireOp",EDGE,"E4")}),1.0]])]});
            var sketch = newSketch(context, id + "F5", { "sketchPlane" : qUnion([Q0])});
            skCircle(sketch, "E22", {"center": v(0, 0) * mm, "radius": 15.88 * mm});
            skSolve(sketch);
        }
        {
            var Q0;
            Q0=qSketchRegion(id+"F5",true);
            extrude(context, id + "F6", {"entities" : qUnion([Q0]), "operationType" : NewBodyOperationType.REMOVE, "depth" : 57.15 * mm});
        }
        {
            var Q0;
            Q0=qCreatedBy(makeId("Right.planeOp"),FACE);
            cPlane(context, id + "F7", {"entities" : qUnion([Q0]), "cplaneType" : CPlaneType.OFFSET, "offset" : 28.57 * mm, "width" : 152.4 * mm, "height" : 152.4 * mm});
        }
        {
            var Q0;
            Q0=qCreatedBy(makeId("Top.planeOp"),FACE);
            cPlane(context, id + "F8", {"entities" : qUnion([Q0]), "cplaneType" : CPlaneType.OFFSET, "offset" : 28.57 * mm, "width" : 152.4 * mm, "height" : 152.4 * mm});
        }
        {
            var Q0;
            Q0=qCreatedBy(id+"F8.planeOp",FACE);
            var sketch = newSketch(context, id + "F9", { "sketchPlane" : qUnion([Q0])});
            skCircle(sketch, "E23", {"center": v(0, -44.45) * mm, "radius": 6.35 * mm});
            skSolve(sketch);
        }
        {
            var Q0;
            Q0=makeQuery(id+"F9.imprint","IMPRINT",FACE,{"disambiguationData":[TD([[makeQuery(id+"F9.imprint","IMPRINT",EDGE,{"derivedFrom":sQuery(id+"F9.wireOp",EDGE,"E23")}),1.0]])]});
            extrude(context, id + "F10", {"entities" : qUnion([Q0]), "operationType" : NewBodyOperationType.REMOVE, "oppositeDirection" : true, "depth" : 63.5 * mm});
        }
        {
            var Q0;
            Q0=makeQuery(id+"F0.imprint","IMPRINT",FACE,{"disambiguationData":[TD([[makeQuery(id+"F0.imprint","IMPRINT",EDGE,{"derivedFrom":sQuery(id+"F0.wireOp",EDGE,"E0")}),1.0]])]});
            var sketch = newSketch(context, id + "F11", { "sketchPlane" : qUnion([Q0])});
            skCircle(sketch, "E24", {"center": v(0, -88.9) * mm, "radius": 3.18 * mm});
            skCircle(sketch, "E25.MirrorC", {"center": v(0, 88.9) * mm, "radius": 3.18 * mm});
            skSolve(sketch);
        }
        {
            var Q0;
            Q0=qSketchRegion(id+"F11",true);
            extrude(context, id + "F12", {"entities" : qUnion([Q0]), "operationType" : NewBodyOperationType.REMOVE, "depth" : 25.4 * mm});
        }
    });
